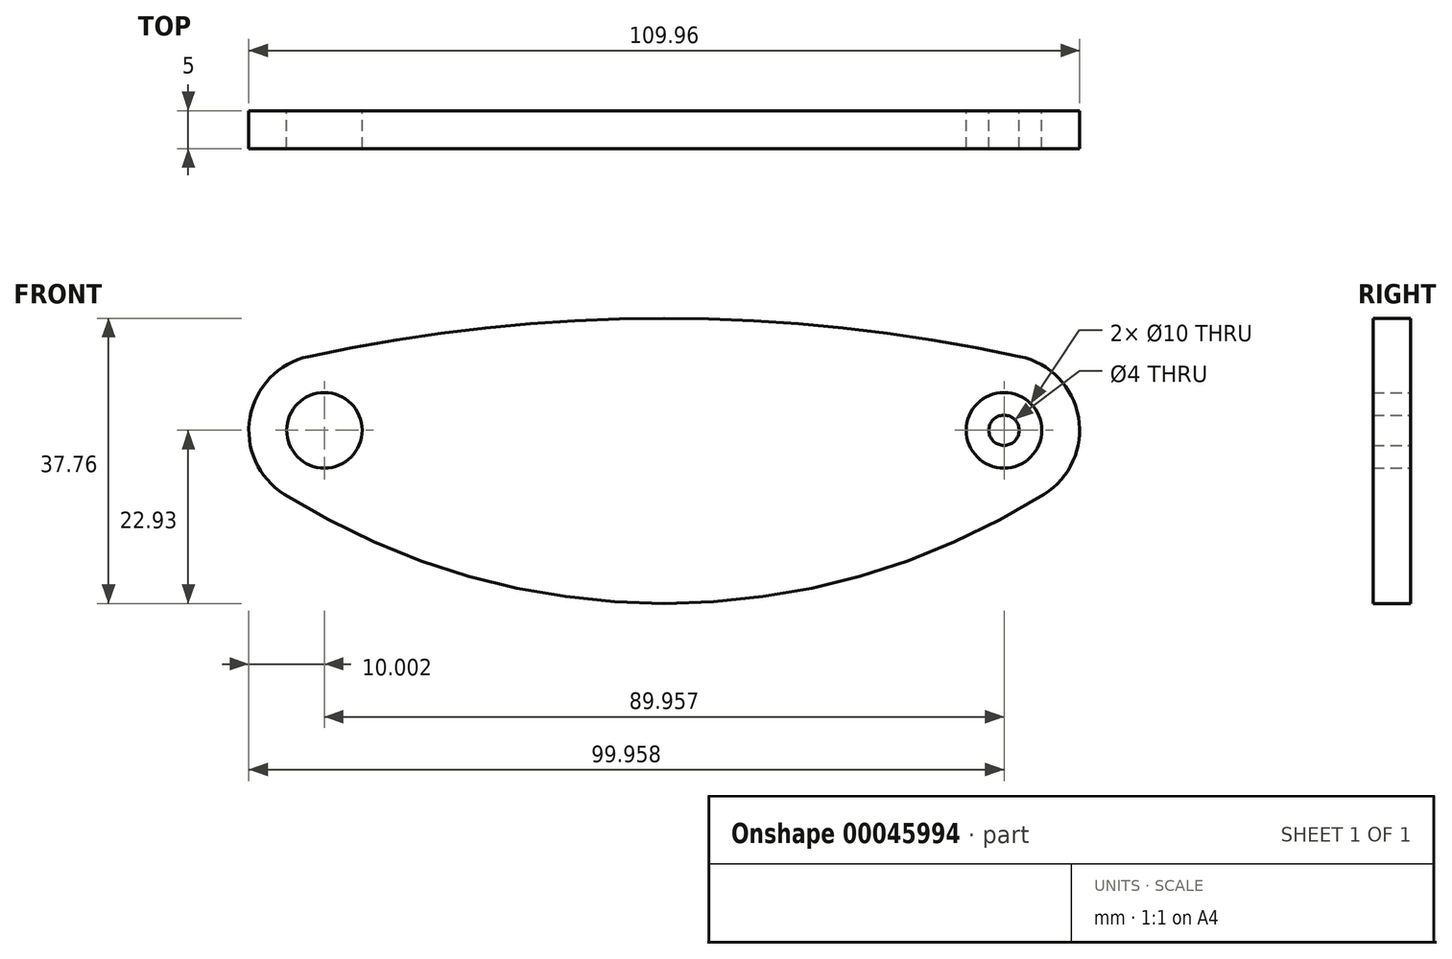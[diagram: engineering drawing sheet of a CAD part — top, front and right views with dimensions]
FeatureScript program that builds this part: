
annotation { "Feature Type Name" : "Feature", "Feature Type Description" : "" }
export const myFeature = defineFeature(function(context is Context, id is Id, definition is map)
    precondition{}
    {
        {
            var Q0;
            Q0=qCreatedBy(makeId("Front.planeOp"),FACE);
            var sketch = newSketch(context, id + "F0", { "sketchPlane" : qUnion([Q0])});
            skLineSegment(sketch, "E0", {"start": v(-44.98, 0) * mm, "end": v(44.98, 0) * mm, "construction": true});
            skCircle(sketch, "E1", {"center": v(-44.98, 0) * mm, "radius": 2 * mm});
            skCircle(sketch, "E2", {"center": v(-44.98, 0) * mm, "radius": 5 * mm});
            skCircle(sketch, "E3", {"center": v(44.98, 0) * mm, "radius": 2 * mm});
            skCircle(sketch, "E4", {"center": v(44.98, 0) * mm, "radius": 5 * mm});
            skArc(sketch, "E5", {"start": v(-50.3, -8.47) * mm, "mid": v(-54.83, 1.72) * mm, "end": v(-47.1, 9.77) * mm});
            skArc(sketch, "E6", {"start": v(50.3, -8.47) * mm, "mid": v(54.83, 1.72) * mm, "end": v(47.1, 9.77) * mm});
            skLineSegment(sketch, "E7", {"start": v(-47.1, 9.77) * mm, "end": v(0, 20) * mm, "construction": true});
            skLineSegment(sketch, "E8", {"start": v(0, 20) * mm, "end": v(47.1, 9.77) * mm, "construction": true});
            skLineSegment(sketch, "E9", {"start": v(-50.3, -8.47) * mm, "end": v(0, -40) * mm, "construction": true});
            skLineSegment(sketch, "E10", {"start": v(0, -40) * mm, "end": v(50.3, -8.47) * mm, "construction": true});
            skArc(sketch, "E11", {"start": v(-47.1, 9.77) * mm, "mid": v(0, 14.83) * mm, "end": v(47.1, 9.77) * mm});
            skArc(sketch, "E12", {"start": v(-50.3, -8.47) * mm, "mid": v(0, -22.93) * mm, "end": v(50.3, -8.47) * mm});
            skSolve(sketch);
        }
        {
            var Q0;
            Q0=makeQuery(id+"F0.imprint","IMPRINT",FACE,{"disambiguationData":[TD([[makeQuery(id+"F0.imprint","IMPRINT",EDGE,{"derivedFrom":sQuery(id+"F0.wireOp",EDGE,"E3")}),-1.0]])]});
            extrude(context, id + "F1", {"entities" : qUnion([Q0]), "depth" : 5 * mm});
        }
        {
            var Q0;
            Q0=makeQuery(id+"F0.imprint","IMPRINT",FACE,{"disambiguationData":[TD([[makeQuery(id+"F0.imprint","IMPRINT",EDGE,{"derivedFrom":sQuery(id+"F0.wireOp",EDGE,"E2")}),-1.0]])]});
            extrude(context, id + "F2", {"entities" : qUnion([Q0]), "depth" : 5 * mm});
        }
    });
